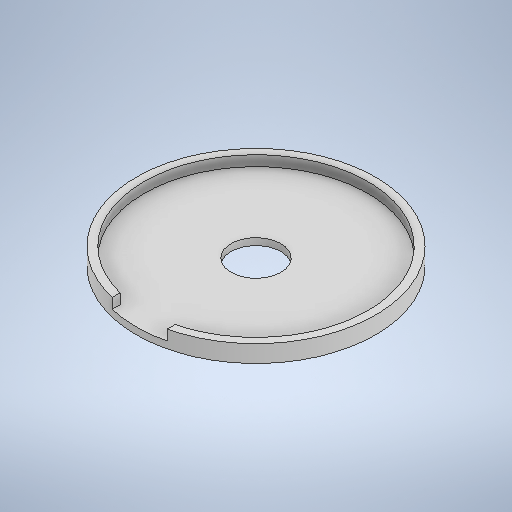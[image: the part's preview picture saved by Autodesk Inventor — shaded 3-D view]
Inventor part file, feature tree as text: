
AUTODESK INVENTOR PART (.ipt)
format: ipt  version: 2025.1 (Build 291241000, 241)  size: 264,192 bytes
history: native  units: mm
features: extrude x4, sketch x4
ambient origin geometry x8: Origin, YZ Plane, XZ Plane, XY Plane, X Axis, Y Axis, Z Axis, Center Point
bodies: Volumenkörper1 (feature_tree)
feature tree (8):
  extrude  "Extrusion1"  Depth=5.0mm TaperAngle=0.0deg
  extrude  "Extrusion2"  Depth=3.0mm TaperAngle=0.0deg
  extrude  "Extrusion3"  TaperAngle=0.0deg  [1 undecoded]
  extrude  "Extrusion4"  Depth=16.0mm
  sketch  "Skizze1"  dims[d0=69.55mm d1=5.0mm d2=0.0mm]
  sketch  "Skizze2"  dims[d3=65.08mm d4=3.0mm d5=0.0mm]
  sketch  "Skizze3"  dims[d6=14.5mm d7=0.0mm d8=0.0mm]
  sketch  "Skizze4"  dims[d9=16.0mm d10=16.0mm d11=10.0mm d12=0.0mm]
note: 1 required parameter value undecoded (feature->parameter linkage not recoverable at this tier; creation-order binding heuristic only, values carry confidence <= 0.55)
